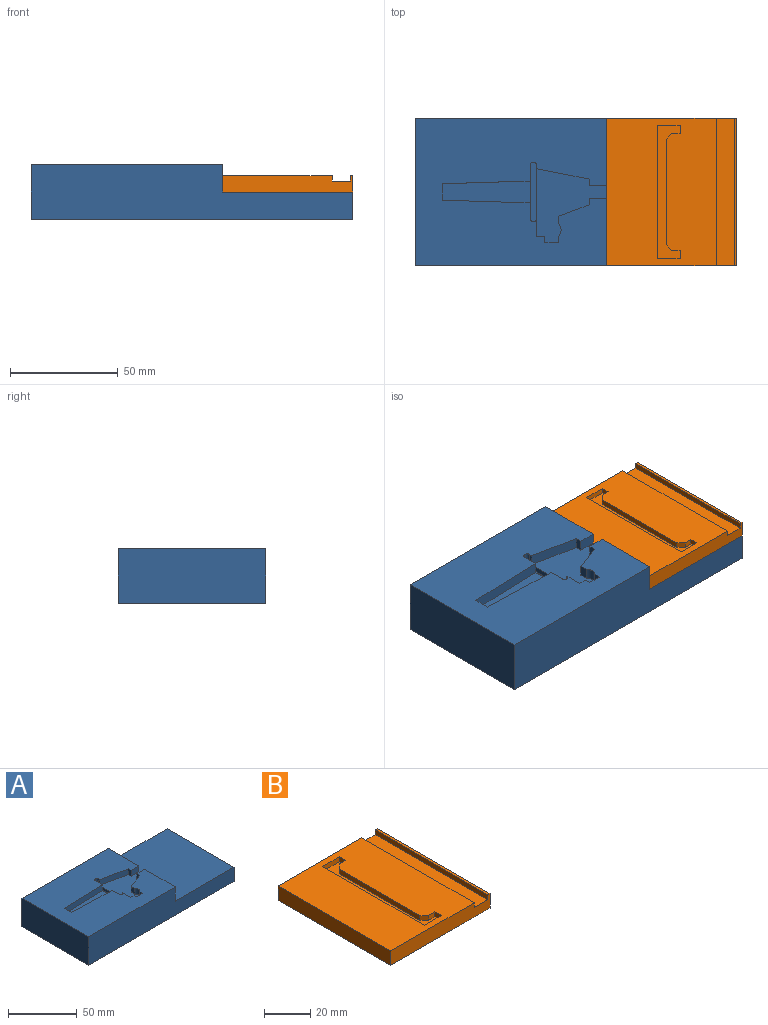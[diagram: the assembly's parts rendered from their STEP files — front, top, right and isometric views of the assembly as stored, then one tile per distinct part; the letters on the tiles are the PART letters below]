
ASSEMBLY  parts=2 mates=1
PART A: 39 faces, bbox 149.4x68.6x25.4 mm
  f0: plane 88.9x68.58mm, normal (0,0,1), area 5045.4mm2, adj f1,f2,f6,f7,f8,f9,f10,f12
  f1: plane 68.58x12.7mm, normal (1,0,0), area 841.3mm2, adj f0,f5,f6,f7,f22,f23,f25
  f2: plane 68.58x25.4mm, normal (-1,0,0), area 1741.9mm2, adj f0,f3,f6,f7
  f3: plane 149.35x68.58mm, normal (0,0,-1), area 10202.8mm2, adj f2,f4,f6,f7,f32,f34,f36,f38
  f4: plane 68.58x12.7mm, normal (1,0,0), area 871mm2, adj f3,f5,f6,f7
  f5: plane 68.58x60.45mm, normal (0,0,1), area 4145.8mm2, adj f1,f4,f6,f7
  f6: plane 149.35x25.4mm, normal (0,1,0), area 3025.8mm2, adj f0,f1,f2,f3,f4,f5
  f7: plane 149.35x25.4mm, normal (0,-1,0), area 3025.8mm2, adj f0,f1,f2,f3,f4,f5
  f8: plane 7.62x5.08mm, normal (1,0,0), area 38.7mm2, adj f0,f9,f10,f11
  f9: plane 40.64x5.08mm, normal (0.03,1,0), area 206.6mm2, adj f0,f8,f11,f26
  f10: plane 40.64x5.08mm, normal (0.03,-1,0), area 206.6mm2, adj f0,f8,f11,f26
  f11: plane 40.64x10.16mm, normal (0,0,1), area 361.3mm2, adj f8,f9,f10,f26
  f12: plane 24.38x5.08mm, normal (-0.19,-0.98,0), area 126.3mm2, adj f0,f24,f25,f27
  f13: plane 8.38x5.08mm, normal (1,0,0), area 42.6mm2, adj f0,f14,f25,f29
  f14: plane 5.08x3.81mm, normal (0,1,0), area 19.4mm2, adj f0,f13,f15,f25
  f15: plane 5.08x2.79mm, normal (1,0,0), area 14.2mm2, adj f0,f14,f16,f25
  f16: plane 6.35x5.08mm, normal (0,1,0), area 32.3mm2, adj f0,f15,f17,f25
  f17: plane 5.08x3.05mm, normal (-1,0,0), area 15.5mm2, adj f0,f16,f18,f25
  f18: cylinder r=3.71mm len=5.59mm, axis (0,0,1), area 32.1mm2, adj f0,f17,f19,f25
  f19: plane 5.08x3.56mm, normal (-1,0,0), area 18.1mm2, adj f0,f18,f20,f25
  f20: plane 14.22x5.33mm, normal (-0.35,0.94,0), area 77.2mm2, adj f0,f19,f21,f25
  f21: plane 5.08x3.05mm, normal (-1,0,0), area 15.5mm2, adj f0,f20,f22,f25
  f22: plane 8.13x5.08mm, normal (0,1,0), area 41.3mm2, adj f0,f1,f21,f25
  f23: plane 8.13x5.08mm, normal (0,-1,0), area 41.3mm2, adj f0,f1,f24,f25
  f24: plane 5.08x3.05mm, normal (-1,0,0), area 15.5mm2, adj f0,f12,f23,f25
  f25: plane 34.29x32.51mm, normal (0,0,1), area 607.7mm2, adj f1,f12,f13,f14,f15,f16,f17,f18
  f26: plane 24.64x7.62mm, normal (1,0,0), area 136.1mm2, adj f0,f9,f10,f11,f28,f29,f30
  f27: plane 24.64x7.62mm, normal (-1,0,0), area 70.3mm2, adj f0,f12,f25,f28,f29,f30
  f28: cylinder r=1.52mm len=7.62mm, axis (0,0,1), area 36.5mm2, adj f0,f26,f27,f30
  f29: cylinder r=1.52mm len=7.62mm, axis (0,0,1), area 36.5mm2, adj f0,f13,f26,f27,f30
  f30: plane 27.69x3.05mm, normal (0,0,1), area 82.4mm2, adj f26,f27,f28,f29
  f31: cone r=0mm half-angle=59deg, axis (0,0,-1), area 11.6mm2, adj f32
  f32: cylinder r=1.78mm len=7.62mm, axis (0,0,-1), area 85.1mm2, adj f3,f31
  f33: cone r=0mm half-angle=59deg, axis (0,0,-1), area 11.6mm2, adj f34
  f34: cylinder r=1.78mm len=7.62mm, axis (0,0,-1), area 85.1mm2, adj f3,f33
  f35: cone r=0mm half-angle=59deg, axis (0,0,-1), area 11.6mm2, adj f36
  f36: cylinder r=1.78mm len=7.62mm, axis (0,0,-1), area 85.1mm2, adj f3,f35
  f37: cone r=0mm half-angle=59deg, axis (0,0,-1), area 11.6mm2, adj f38
  f38: cylinder r=1.78mm len=7.62mm, axis (0,0,-1), area 85.1mm2, adj f3,f37
PART B: 21 faces, bbox 60.5x68.6x7.6 mm
  f0: plane 68.58x2.54mm, normal (1,0,0), area 174.2mm2, adj f1,f7,f8,f9
  f1: plane 68.58x50.8mm, normal (0,0,1), area 3190.9mm2, adj f0,f2,f8,f9,f10,f11,f12,f13
  f2: plane 68.58x7.62mm, normal (-1,0,0), area 522.6mm2, adj f1,f3,f8,f9
  f3: plane 68.58x60.45mm, normal (0,0,-1), area 4145.8mm2, adj f2,f4,f8,f9
  f4: plane 68.58x7.62mm, normal (1,0,0), area 522.6mm2, adj f3,f5,f8,f9
  f5: plane 68.58x1.27mm, normal (0,0,1), area 87.1mm2, adj f4,f6,f8,f9
  f6: plane 68.58x2.54mm, normal (-1,0,0), area 174.2mm2, adj f5,f7,f8,f9
  f7: plane 68.58x8.38mm, normal (0,0,1), area 574.8mm2, adj f0,f6,f8,f9
  f8: plane 60.45x7.62mm, normal (0,1,0), area 439.4mm2, adj f0,f1,f2,f3,f4,f5,f6,f7
  f9: plane 60.45x7.62mm, normal (0,-1,0), area 439.4mm2, adj f0,f1,f2,f3,f4,f5,f6,f7
  f10: plane 10.31x2.54mm, normal (0,-1,0), area 26.2mm2, adj f1,f11,f19,f20
  f11: plane 61.98x2.54mm, normal (1,0,0), area 157.4mm2, adj f1,f10,f12,f20
  f12: plane 10.31x2.54mm, normal (0,1,0), area 26.2mm2, adj f1,f11,f13,f20
  f13: plane 3.81x2.54mm, normal (-1,0,0), area 9.7mm2, adj f1,f12,f14,f20
  f14: plane 3.81x2.54mm, normal (0,-1,0), area 9.7mm2, adj f1,f13,f15,f20
  f15: plane 2.69x2.69mm, normal (-0.71,-0.71,0), area 9.7mm2, adj f1,f14,f16,f20
  f16: plane 48.97x2.54mm, normal (-1,0,0), area 124.4mm2, adj f1,f15,f17,f20
  f17: plane 2.69x2.69mm, normal (-0.71,0.71,0), area 9.7mm2, adj f1,f16,f18,f20
  f18: plane 3.81x2.54mm, normal (0,1,0), area 9.7mm2, adj f1,f17,f19,f20
  f19: plane 3.81x2.54mm, normal (-1,0,0), area 9.7mm2, adj f1,f10,f18,f20
  f20: plane 61.98x10.31mm, normal (0,0,1), area 292.9mm2, adj f10,f11,f12,f13,f14,f15,f16,f17
PLACE A t=(25.84,-3.31,38)mm
PLACE B t=(25.84,-3.31,38)mm
MATE parallel A.f5 <-> B.f3  axis (0,0,1) through (-4.39,30.98,50.7)mm
